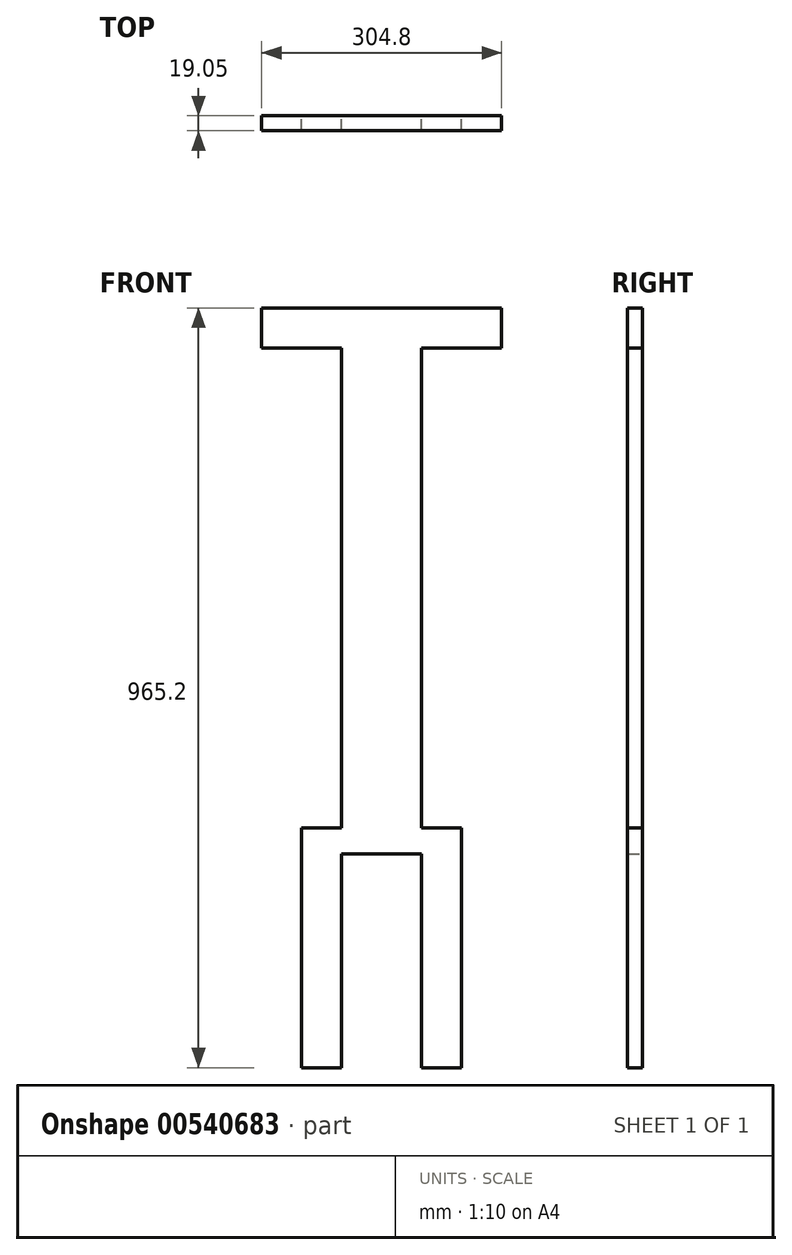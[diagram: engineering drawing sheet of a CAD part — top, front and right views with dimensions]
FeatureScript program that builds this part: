
annotation { "Feature Type Name" : "Feature", "Feature Type Description" : "" }
export const myFeature = defineFeature(function(context is Context, id is Id, definition is map)
    precondition{}
    {
        {
            var Q0;
            Q0=qCreatedBy(makeId("Front.planeOp"),FACE);
            var sketch = newSketch(context, id + "F0", { "sketchPlane" : qUnion([Q0])});
            skLineSegment(sketch, "E0", {"start": v(-109.83, 101.92) * mm, "end": v(-160.63, 101.92) * mm});
            skLineSegment(sketch, "E1", {"start": v(-8.23, 101.92) * mm, "end": v(42.57, 101.92) * mm});
            skLineSegment(sketch, "E2", {"start": v(42.57, 101.92) * mm, "end": v(42.57, -202.88) * mm});
            skLineSegment(sketch, "E3", {"start": v(-160.63, 101.92) * mm, "end": v(-160.63, -202.88) * mm});
            skLineSegment(sketch, "E4", {"start": v(-160.63, -202.88) * mm, "end": v(-109.83, -202.88) * mm});
            skLineSegment(sketch, "E5", {"start": v(-8.23, -202.88) * mm, "end": v(42.57, -202.88) * mm});
            skLineSegment(sketch, "E6", {"start": v(-8.23, 68.75) * mm, "end": v(-109.83, 68.75) * mm});
            skLineSegment(sketch, "E7", {"start": v(-109.83, 711.52) * mm, "end": v(-211.43, 711.52) * mm});
            skLineSegment(sketch, "E8", {"start": v(-8.23, 711.52) * mm, "end": v(93.37, 711.52) * mm});
            skLineSegment(sketch, "E9", {"start": v(93.37, 711.52) * mm, "end": v(93.37, 762.32) * mm});
            skLineSegment(sketch, "E10", {"start": v(-211.43, 711.52) * mm, "end": v(-211.43, 762.32) * mm});
            skLineSegment(sketch, "E11", {"start": v(-211.43, 762.32) * mm, "end": v(93.37, 762.32) * mm});
            skLineSegment(sketch, "E12", {"start": v(-8.23, 68.75) * mm, "end": v(-8.23, -202.88) * mm});
            skLineSegment(sketch, "E13", {"start": v(-8.23, 101.92) * mm, "end": v(-8.23, 711.52) * mm});
            skLineSegment(sketch, "E14", {"start": v(-109.83, -202.88) * mm, "end": v(-109.83, 68.75) * mm});
            skLineSegment(sketch, "E15", {"start": v(-109.83, 101.92) * mm, "end": v(-109.83, 711.52) * mm});
            skSolve(sketch);
        }
        {
            var Q0;
            Q0 = qSketchRegion(id + "F0", true);
            extrude(context, id + "F1", {"entities" : qUnion([Q0]), "depth" : 19.05 * mm, "offsetDistance" : 25.4 * mm});
        }
    });
